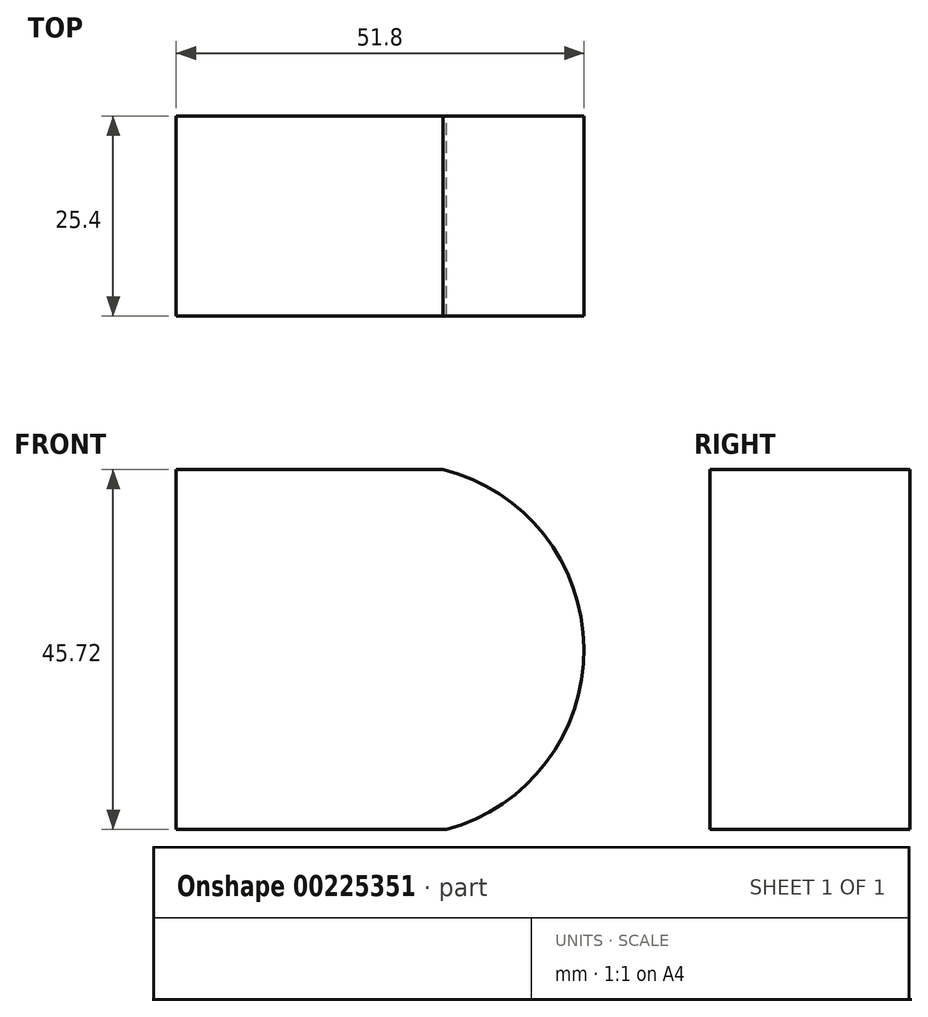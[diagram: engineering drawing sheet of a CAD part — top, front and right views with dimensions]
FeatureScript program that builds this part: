
annotation { "Feature Type Name" : "Feature", "Feature Type Description" : "" }
export const myFeature = defineFeature(function(context is Context, id is Id, definition is map)
    precondition{}
    {
        {
            var Q0;
            Q0=qCreatedBy(makeId("Front.planeOp"),FACE);
            var sketch = newSketch(context, id + "F0", { "sketchPlane" : qUnion([Q0])});
            skLineSegment(sketch, "E0.bottom", {"start": v(-31.86, 15.43) * mm, "end": v(35.86, 15.43) * mm});
            skLineSegment(sketch, "E0.top", {"start": v(-31.86, -30.29) * mm, "end": v(35.86, -30.29) * mm});
            skLineSegment(sketch, "E0.left", {"start": v(-31.86, 15.43) * mm, "end": v(-31.86, -30.29) * mm});
            skLineSegment(sketch, "E0.right", {"start": v(35.86, 15.43) * mm, "end": v(35.86, -30.29) * mm});
            skArc(sketch, "E1", {"start": v(-9.81, -30.29) * mm, "mid": v(19.18, -13.4) * mm, "end": v(2, 15.43) * mm});
            skSolve(sketch);
        }
        {
            var Q0;
            {var subQ0=sQuery(id+"F0.wireOp",EDGE,"E0.left");Q0=makeQuery(id+"F0.imprint","IMPRINT",FACE,{"disambiguationData":[TD([[makeQuery(id+"F0.imprint","IMPRINT",EDGE,{"derivedFrom":subQ0}),1.0]])]});}
            extrude(context, id + "F1", {"entities" : qUnion([Q0]), "depth" : 25.4 * mm});
        }
    });
